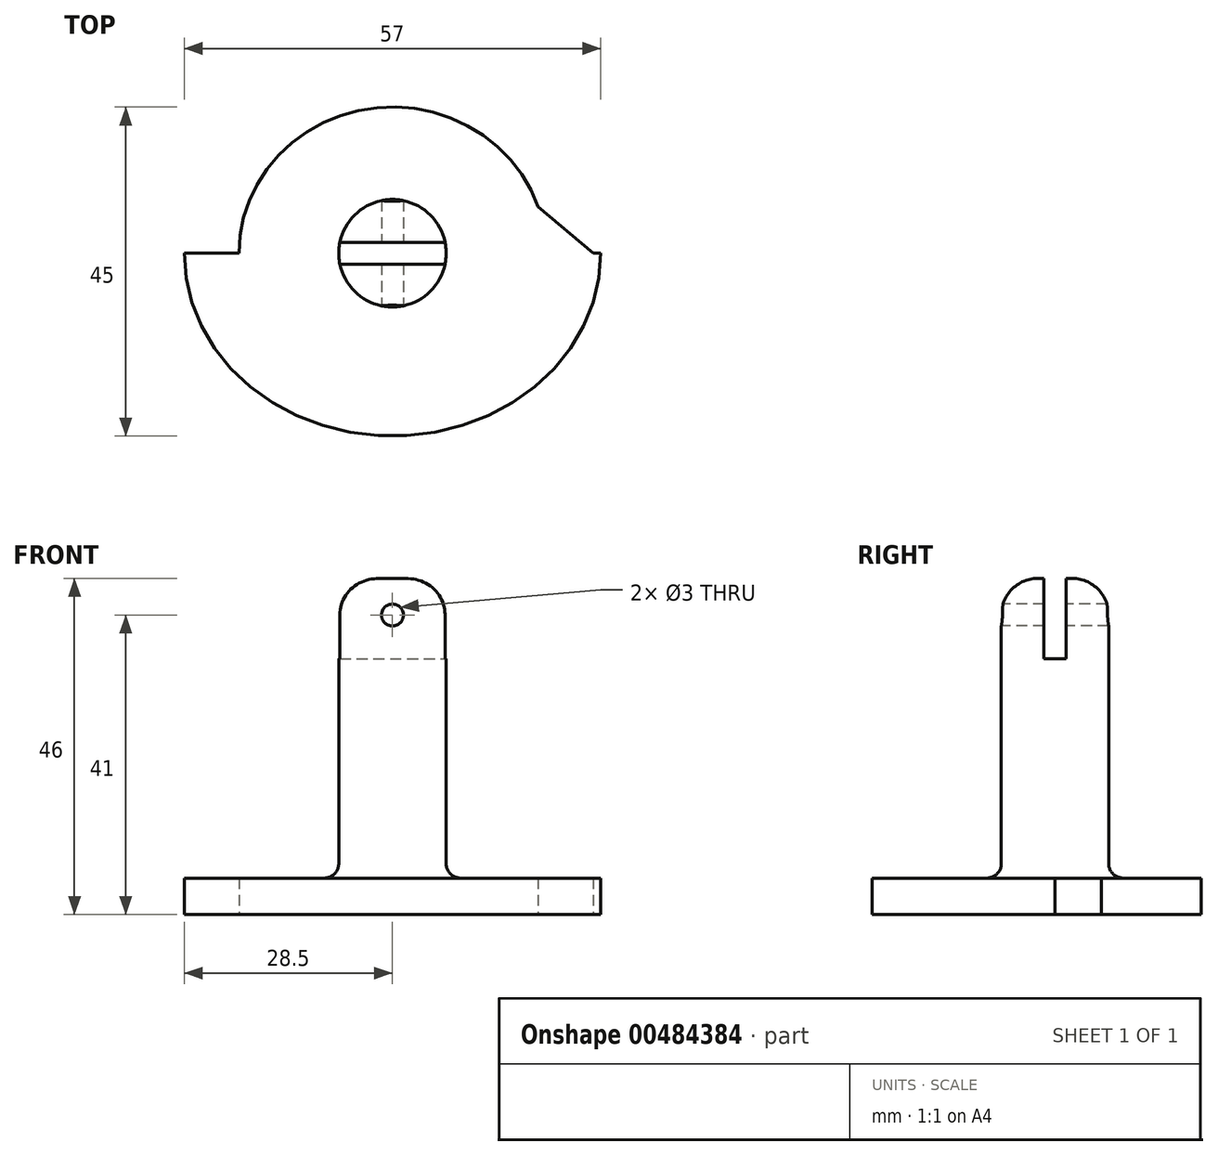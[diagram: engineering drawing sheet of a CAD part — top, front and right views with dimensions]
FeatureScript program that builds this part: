
annotation { "Feature Type Name" : "Feature", "Feature Type Description" : "" }
export const myFeature = defineFeature(function(context is Context, id is Id, definition is map)
    precondition{}
    {
        {
            var Q0;
            Q0=qCreatedBy(makeId("Top.planeOp"),FACE);
            var sketch = newSketch(context, id + "F0", { "sketchPlane" : qUnion([Q0])});
            skEllipse(sketch, "E0", {"center": v(0, 0) * mm, "majorRadius": 28.5 * mm, "minorRadius": 25 * mm, "majorAxis": v(1, 0)});
            skEllipse(sketch, "E1", {"center": v(0, 0) * mm, "majorRadius": 21 * mm, "minorRadius": 20 * mm, "majorAxis": v(-1, 0)});
            skLineSegment(sketch, "E2", {"start": v(-28.5, 0) * mm, "end": v(-21, 0) * mm});
            skLineSegment(sketch, "E3", {"start": v(21, 0) * mm, "end": v(28.5, 0) * mm});
            skCircle(sketch, "E4", {"center": v(0, 0) * mm, "radius": 7.35 * mm});
            skCircle(sketch, "E5", {"center": v(0, 0) * mm, "radius": 9 * mm});
            skLineSegment(sketch, "E6", {"start": v(27.5, 0) * mm, "end": v(19.9, 6.37) * mm});
            skSolve(sketch);
        }
        {
            var Q0;
            {var subQ0=sQuery(id+"F0.wireOp",EDGE,"E1");var subQ1=makeQuery(id+"F0.imprint","INTERSECT",VERTEX,{"derivedFrom":[subQ0,sQuery(id+"F0.wireOp",EDGE,"E2")]});Q0=makeQuery(id+"F0.imprint","IMPRINT",FACE,{"disambiguationData":[TD([[makeQuery(id+"F0.imprint","IMPRINT",EDGE,{"disambiguationData":[TD([[subQ1,-1.0]])],"derivedFrom":subQ0}),1.0]])]});}
            var Q1;
            {var subQ0=sQuery(id+"F0.wireOp",EDGE,"E2");Q1=makeQuery(id+"F0.imprint","IMPRINT",FACE,{"disambiguationData":[TD([[makeQuery(id+"F0.imprint","IMPRINT",EDGE,{"derivedFrom":subQ0}),-1.0]])]});}
            var Q2;
            {var subQ0=sQuery(id+"F0.wireOp",EDGE,"veYjzUdA-I342-z0th-yNIf-FmOSI8J3daDo");Q2=makeQuery(id+"F0.imprint","IMPRINT",FACE,{"disambiguationData":[TD([[makeQuery(id+"F0.imprint","IMPRINT",EDGE,{"derivedFrom":subQ0}),1.0]])]});}
            var Q3;
            Q3=makeQuery(id+"F0.imprint","IMPRINT",FACE,{"disambiguationData":[TD([[makeQuery(id+"F0.imprint","IMPRINT",EDGE,{"derivedFrom":sQuery(id+"F0.wireOp",EDGE,"E4")}),1.0]])]});
            var Q4;
            Q4=makeQuery(id+"F0.imprint","IMPRINT",FACE,{"disambiguationData":[TD([[makeQuery(id+"F0.imprint","IMPRINT",EDGE,{"derivedFrom":sQuery(id+"F0.wireOp",EDGE,"E4")}),-1.0]])]});
            var Q5;
            {var subQ3=sQuery(id+"F0.wireOp",EDGE,"E6");Q5=makeQuery(id+"F0.imprint","IMPRINT",FACE,{"disambiguationData":[TD([[makeQuery(id+"F0.imprint","IMPRINT",EDGE,{"derivedFrom":subQ3}),1.0]])]});}
            extrude(context, id + "F1", {"entities" : qUnion([Q0, Q1, Q2, Q3, Q4, Q5]), "depth" : 5 * mm, "offsetDistance" : 25 * mm});
        }
        {
            var Q0;
            Q0=makeQuery(id+"F0.imprint","IMPRINT",FACE,{"disambiguationData":[TD([[makeQuery(id+"F0.imprint","IMPRINT",EDGE,{"derivedFrom":sQuery(id+"F0.wireOp",EDGE,"E4")}),1.0]])]});
            extrude(context, id + "F2", {"entities" : qUnion([Q0]), "operationType" : NewBodyOperationType.ADD, "depth" : 46 * mm, "offsetDistance" : 25 * mm});
        }
        {
            var Q0;
            Q0=makeQuery(id+"F2.opExtrude","CAP_FACE",FACE,{"disambiguationData":[OSD([sQuery(id+"F0.wireOp",EDGE,"E4")])],"isStart":false});
            var sketch = newSketch(context, id + "F3", { "sketchPlane" : qUnion([Q0])});
            skLineSegment(sketch, "E7.bottom", {"start": v(-7.2, 1.5) * mm, "end": v(7.2, 1.5) * mm});
            skLineSegment(sketch, "E7.top", {"start": v(-7.2, -1.5) * mm, "end": v(7.2, -1.5) * mm});
            skLineSegment(sketch, "E7.left", {"start": v(-7.2, 1.5) * mm, "end": v(-7.2, -1.5) * mm});
            skLineSegment(sketch, "E7.right", {"start": v(7.2, 1.5) * mm, "end": v(7.2, -1.5) * mm});
            skSolve(sketch);
        }
        {
            var Q0;
            Q0=makeQuery(id+"F3.imprint","IMPRINT",FACE,{"disambiguationData":[TD([[makeQuery(id+"F3.imprint","IMPRINT",EDGE,{"derivedFrom":sQuery(id+"F3.wireOp",EDGE,"E7.bottom")}),-1.0]])]});
            var Q1;
            {var subQ0=sQuery(id+"F3.wireOp",EDGE,"E7.left");Q1=makeQuery(id+"F3.imprint","IMPRINT",FACE,{"disambiguationData":[TD([[makeQuery(id+"F3.imprint","IMPRINT",EDGE,{"derivedFrom":subQ0}),-1.0]])]});}
            var Q2;
            {var subQ0=sQuery(id+"F3.wireOp",EDGE,"E7.right");Q2=makeQuery(id+"F3.imprint","IMPRINT",FACE,{"disambiguationData":[TD([[makeQuery(id+"F3.imprint","IMPRINT",EDGE,{"derivedFrom":subQ0}),1.0]])]});}
            extrude(context, id + "F4", {"entities" : qUnion([Q0, Q1, Q2]), "operationType" : NewBodyOperationType.REMOVE, "oppositeDirection" : true, "depth" : 11 * mm, "offsetDistance" : 25 * mm});
        }
        {
            var Q0;
            {var subQ0=sQuery(id+"F0.wireOp",EDGE,"E4");Q0=makeQuery(id+"F4.boolean.opBoolean","SPLIT",EDGE,{"disambiguationData":[TD([makeQuery(id+"F4.opExtrude","SWEPT_FACE",FACE,{"disambiguationData":[OSD([sQuery(id+"F3.wireOp",EDGE,"E7.top")])]})])],"derivedFrom":makeQuery(id+"F2.opExtrude","CAP_EDGE",EDGE,{"disambiguationData":[OSD([subQ0])],"isStart":false})});}
            var Q1;
            {var subQ0=sQuery(id+"F0.wireOp",EDGE,"E4");Q1=makeQuery(id+"F4.boolean.opBoolean","SPLIT",EDGE,{"disambiguationData":[TD([makeQuery(id+"F4.opExtrude","SWEPT_FACE",FACE,{"disambiguationData":[OSD([sQuery(id+"F3.wireOp",EDGE,"E7.bottom")])]})])],"derivedFrom":makeQuery(id+"F2.opExtrude","CAP_EDGE",EDGE,{"disambiguationData":[OSD([subQ0])],"isStart":false})});}
            fillet(context, id + "F5", {"entities" : qUnion([Q0, Q1]), "radius" : 5 * mm, "tangentPropagation" : true, "allowEdgeOverflow" : false});
        }
        {
            var Q0;
            Q0=makeQuery(id+"F4.boolean.opBoolean","COPY",FACE,{"derivedFrom":makeQuery(id+"F4.opExtrude","SWEPT_FACE",FACE,{"disambiguationData":[OSD([sQuery(id+"F3.wireOp",EDGE,"E7.bottom")])]})});
            var sketch = newSketch(context, id + "F6", { "sketchPlane" : qUnion([Q0])});
            skCircle(sketch, "E8", {"center": v(0, 41) * mm, "radius": 1.5 * mm});
            skSolve(sketch);
        }
        {
            var Q0;
            Q0=makeQuery(id+"F6.imprint","IMPRINT",FACE,{"disambiguationData":[TD([[makeQuery(id+"F6.imprint","IMPRINT",EDGE,{"derivedFrom":sQuery(id+"F6.wireOp",EDGE,"E8")}),1.0]])]});
            extrude(context, id + "F7", {"entities" : qUnion([Q0]), "operationType" : NewBodyOperationType.REMOVE, "oppositeDirection" : true, "depth" : 25 * mm, "offsetDistance" : 25 * mm, "hasSecondDirection" : true, "secondDirectionOppositeDirection" : false, "secondDirectionDepth" : 25 * mm});
        }
        {
            var Q0;
            Q0=makeQuery(id+"F2.boolean.opBoolean","INTERSECT",EDGE,{"derivedFrom":[makeQuery(id+"F1.opExtrude","CAP_FACE",FACE,{"disambiguationData":[OSD([sQuery(id+"F0.wireOp",EDGE,"E0"),sQuery(id+"F0.wireOp",EDGE,"E1"),sQuery(id+"F0.wireOp",EDGE,"E2"),sQuery(id+"F0.wireOp",EDGE,"E3"),sQuery(id+"F0.wireOp",EDGE,"E6")])],"isStart":false}),makeQuery(id+"F2.opExtrude","SWEPT_FACE",FACE,{"disambiguationData":[OSD([sQuery(id+"F0.wireOp",EDGE,"E4")])]})]});
            fillet(context, id + "F8", {"entities" : qUnion([Q0]), "radius" : 2 * mm, "tangentPropagation" : true, "allowEdgeOverflow" : false});
        }
    });
